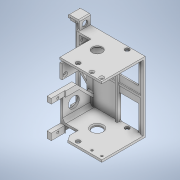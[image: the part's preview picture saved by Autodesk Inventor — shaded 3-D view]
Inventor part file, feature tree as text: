
AUTODESK INVENTOR PART (.ipt)
format: ipt  version: 2021 (Build 250183000, 183)  size: 1,060,352 bytes
history: native  units: mm
features: sketch x66, extrude x55, chamfer x12, hole x11, fillet x7
ambient origin geometry x8: Origin, YZ Plane, XZ Plane, XY Plane, X Axis, Y Axis, Z Axis, Center Point
bodies: Solid1 (feature_tree)
feature tree (151):
  extrude  "Extrusion1"  Depth=48.0mm
  extrude  "Extrusion3"  Depth=2.0mm
  extrude  "Extrusion4"  Depth=2.0mm TaperAngle=0.0deg
  hole  "Hole1"  [1 undecoded]
  hole  "Hole2"  [1 undecoded]
  extrude  "Extrusion5"  Depth=4.0mm
  extrude  "Extrusion6"  Depth=33.0mm
  extrude  "Extrusion7"  Depth=2.0mm
  extrude  "Extrusion8"  Depth=2.0mm TaperAngle=0.0deg
  extrude  "Extrusion9"  Depth=4.0mm
  extrude  "Extrusion10"  Depth=4.0mm
  extrude  "Extrusion11"  Depth=1.0mm
  chamfer  "Chamfer1"  Distance=2.0mm
  fillet  "Fillet1"  Radius=0.4mm
  hole  "Hole3"  [1 undecoded]
  chamfer  "Chamfer2"  Distance=12.4mm
  extrude  "Extrusion12"  Depth=2.0mm TaperAngle=0.0deg
  extrude  "Extrusion13"  Depth=2.0mm TaperAngle=0.0deg
  extrude  "Extrusion14"  Depth=4.4mm
  hole  "Hole4"  [1 undecoded]
  extrude  "Extrusion15"  Depth=2.4mm
  extrude  "Extrusion16"  Depth=1.0mm TaperAngle=45.0deg
  chamfer  "Chamfer3"  Distance=37.6mm
  extrude  "Extrusion17"  Depth=2.0mm TaperAngle=0.0deg
  extrude  "Extrusion18"  Depth=2.4mm
  extrude  "Extrusion19"  Depth=16.0mm
  extrude  "Extrusion20"  Depth=15.0mm
  extrude  "Extrusion21"  Depth=8.0mm TaperAngle=0.0deg
  extrude  "Extrusion22"  Depth=2.0mm TaperAngle=0.0deg
  extrude  "Extrusion23"  Depth=30.0mm
  hole  "Hole5"  [1 undecoded]
  extrude  "Extrusion24"  Depth=20.0mm TaperAngle=0.0deg
  extrude  "Extrusion26"  Depth=2.0mm TaperAngle=0.0deg
  extrude  "Extrusion27"  Depth=9.0mm
  extrude  "Extrusion28"  Depth=3.0mm TaperAngle=0.0deg
  extrude  "Extrusion29"  Depth=6.0mm
  extrude  "Extrusion30"  Depth=2.0mm
  hole  "Hole6"  [1 undecoded]
  chamfer  "Chamfer4"  Distance=17.0mm
  chamfer  "Chamfer5"  Distance=2.0mm
  extrude  "Extrusion32"  Depth=2.0mm
  chamfer  "Chamfer6"  Distance=2.0mm
  extrude  "Extrusion33"  Depth=6.0mm
  fillet  "Fillet2"  Radius=5.0mm
  extrude  "Extrusion34"  TaperAngle=0.0deg  [1 undecoded]
  extrude  "Extrusion35"  Depth=5.0mm TaperAngle=45.0deg
  extrude  "Extrusion36"  Depth=5.0mm
  extrude  "Extrusion37"  Depth=8.0mm TaperAngle=45.0deg
  extrude  "Extrusion38"  Depth=3.0mm
  fillet  "Fillet3"  Radius=10.0mm
  extrude  "Extrusion39"  Depth=10.0mm
  fillet  "Fillet4"  Radius=2.0mm
  extrude  "Extrusion40"  Depth=0.5mm
  extrude  "Extrusion41"  Depth=12.4mm TaperAngle=0.0deg
  extrude  "Extrusion42"  Depth=2.0mm
  extrude  "Extrusion43"  Depth=10.0mm
  hole  "Hole7"  [1 undecoded]
  hole  "Hole8"  [1 undecoded]
  hole  "Hole9"  [1 undecoded]
  hole  "Hole10"  [1 undecoded]
  extrude  "Extrusion44"  Depth=2.0mm TaperAngle=0.0deg
  chamfer  "Chamfer7"  Distance=2.0mm
  extrude  "Extrusion45"  Depth=5.0mm TaperAngle=0.0deg
  extrude  "Extrusion46"  Depth=10.0mm
  extrude  "Extrusion47"  Depth=10.0mm
  extrude  "Extrusion48"  Depth=2.0mm
  extrude  "Extrusion50"  Depth=9.0mm
  fillet  "Fillet7"  Radius=2.2mm
  extrude  "Extrusion52"  Depth=3.0mm
  chamfer  "Chamfer9"  Distance=3.0mm
  chamfer  "Chamfer10"  Distance=3.0mm
  chamfer  "Chamfer11"  Distance=3.0mm
  extrude  "Extrusion54"  Depth=3.0mm
  extrude  "Extrusion55"  Depth=12.0mm
  extrude  "Extrusion56"  Depth=5.2mm
  extrude  "Extrusion57"  Depth=1.2mm
  chamfer  "Chamfer12"  Distance=1.0mm
  extrude  "Extrusion58"  Depth=1.0mm
  extrude  "Extrusion59"  Depth=2.0mm TaperAngle=0.0deg
  fillet  "Fillet9"  Radius=1.2mm
  hole  "Hole11"  [1 undecoded]
  fillet  "Fillet10"  Radius=81.0mm
  chamfer  "Chamfer13"  Distance=10.0mm
  extrude  "Extrusion60"  Depth=0.5mm
  extrude  "Extrusion61"  Depth=0.5mm
  sketch  "Sketch1"  dims[d0=48.0mm d1=60.0mm]
  sketch  "Sketch3"  dims[d2=1.2mm d3=0.0mm d6=2.0mm]
  sketch  "Sketch4"  dims[d7=2.0mm d8=40.0mm d9=0.0mm]
  sketch  "Sketch5"  dims[d10=16.8mm d11=21.0mm]
  sketch  "Sketch6"  dims[d12=9.2mm d13=80.0mm d14=0.0mm]
  sketch  "Sketch7"  dims[d15=4.0mm d16=22.7mm]
  sketch  "Sketch8"  dims[d17=11.8mm d18=33.0mm]
  sketch  "Sketch9"  dims[d19=4.0mm d20=6.0mm d21=6.0mm d22=2.0mm d23=90.0deg d24=4.0mm d25=20.594885mm]
  sketch  "Sketch10"  dims[d26=4.0mm d27=6.0mm d28=6.0mm d29=2.0mm d30=90.0deg d31=4.0mm d32=20.594885mm d33=2.0mm]
  sketch  "Sketch11"  dims[d34=2.0mm d35=0.8mm d36=0.0mm]
  sketch  "Sketch12"  dims[d37=4.0mm d38=4.0mm]
  sketch  "Sketch13"  dims[d39=1.0mm d40=4.0mm]
  sketch  "Sketch14"  dims[d41=4.0mm d42=1.0mm]
  sketch  "Sketch15"  dims[d43=3.0mm d44=2.0mm d45=0.0mm d46=0.4mm d47=0.0mm]
  sketch  "Sketch16"  dims[d48=12.0mm d49=22.0mm]
  sketch  "Sketch17"  dims[d50=12.4mm d51=12.4mm d52=0.0mm]
  sketch  "Sketch18"  dims[d53=8.0mm d54=2.0mm d55=0.0mm]
  sketch  "Sketch19"  dims[d56=8.0mm d57=2.0mm d58=0.0mm]
  sketch  "Sketch20"  dims[d59=0.4mm d60=4.4mm]
  sketch  "Sketch21"  dims[d61=12.4mm d62=0.0mm d63=2.4mm d64=2.0mm d65=45.0deg]
  sketch  "Sketch22"  dims[d66=2.0mm d67=2.4mm]
  sketch  "Sketch23"  dims[d68=6.0mm]
  sketch  "Sketch24"  dims[d69=2.0mm d70=6.0mm d71=3.0mm d72=2.0mm d73=90.0deg d74=5.0mm d75=20.594885mm d76=1.0mm d77=2.0mm d78=45.0deg]
  sketch  "Sketch25"  dims[d79=22.0mm]
  sketch  "Sketch26"  dims[d80=5.0mm]
  sketch  "Sketch27"  dims[d81=4.4mm]
  sketch  "Sketch28"  dims[d82=4.4mm d83=37.6mm d84=0.0mm]
  sketch  "Sketch29"  dims[d85=4.4mm d86=0.0mm d87=2.0mm d88=0.0mm]
  sketch  "Sketch31"  dims[d89=6.0mm d90=2.4mm]
  sketch  "Sketch32"  dims[d91=27.2mm]
  sketch  "Sketch33"  dims[d92=2.0mm d93=6.0mm d94=3.0mm d95=2.0mm d96=90.0deg d97=5.0mm d98=20.594885mm d99=16.0mm]
  sketch  "Sketch34"  dims[d100=2.0mm d101=0.0mm d102=15.0mm]
  sketch  "Sketch35"  dims[d103=8.0mm d104=20.0mm d105=0.0mm]
  sketch  "Sketch36"  dims[d106=2.0mm d107=2.0mm d108=45.0deg d109=0.8mm d110=0.0mm]
  sketch  "Sketch38"  dims[d111=60.0mm d112=30.0mm]
  sketch  "Sketch39"  dims[d113=1.0mm d114=1.0mm]
  sketch  "Sketch40"  dims[d115=0.8mm d116=0.0mm d117=20.0mm d118=0.0mm]
  sketch  "Sketch41"  dims[d119=20.0mm d120=0.0mm d121=2.0mm d122=0.0mm]
  sketch  "Sketch42"  dims[d123=17.0mm d124=9.0mm]
  sketch  "Sketch43"  dims[d125=10.0mm d126=0.0mm d127=3.0mm d128=0.0mm]
  sketch  "Sketch44"  dims[d129=6.0mm d130=9.6mm]
  sketch  "Sketch45"  dims[d131=2.0mm d132=6.0mm d133=3.0mm d134=2.0mm d135=90.0deg d136=5.0mm d137=20.594885mm d138=2.0mm]
  sketch  "Sketch46"  dims[d139=2.0mm d140=10.0mm d141=0.0mm]
  sketch  "Sketch47"  dims[d145=0.2mm d146=17.0mm d147=0.0mm d148=2.0mm d149=0.0mm]
  sketch  "Sketch48"  dims[d150=11.7mm d151=28.0mm d152=2.0mm d153=0.0mm]
  sketch  "Sketch49"  dims[d154=2.0mm d155=6.0mm d156=5.0mm d157=0.0mm]
  sketch  "Sketch50"  dims[d158=33.4mm d159=0.0mm d160=0.0mm]
  sketch  "Sketch51"  dims[d161=27.2mm]
  sketch  "Sketch52"  dims[d162=2.0mm d163=6.0mm d164=3.0mm d165=2.0mm d166=90.0deg d167=5.0mm d168=20.594885mm d169=5.0mm d170=2.0mm d171=45.0deg]
  sketch  "Sketch53"  dims[d172=5.6mm d173=2.0mm d174=45.0deg d181=5.0mm]
  sketch  "Sketch54"  dims[d182=2.0mm d183=0.0mm d184=8.0mm d185=2.0mm d186=45.0deg]
  sketch  "Sketch55"  dims[d187=20.0mm d188=0.0mm d189=3.0mm d190=10.0mm]
  sketch  "Sketch56"  dims[d191=10.0mm d192=10.0mm d193=2.0mm d194=0.0mm]
  sketch  "Sketch57"  dims[d195=23.0mm d196=0.5mm]
  sketch  "Sketch58"  dims[d197=0.5mm d198=12.4mm d199=0.0mm]
  sketch  "Sketch60"  dims[d200=10.0mm d201=0.0mm d202=2.0mm]
  sketch  "Sketch62"  dims[d203=2.4mm d204=0.0mm d205=10.0mm]
  sketch  "Sketch64"  dims[d206=5.0mm d207=5.0mm d208=0.0mm]
  sketch  "Sketch65"  dims[d209=1.0mm d210=4.0mm]
  sketch  "Sketch66"  dims[d211=4.0mm d212=20.0mm]
  sketch  "Sketch67"  dims[d213=4.0mm d214=4.0mm]
  sketch  "Sketch68"  dims[d215=20.0mm d216=2.0mm d217=0.0mm]
  sketch  "Sketch69"  dims[d218=1.0mm]
  sketch  "Sketch70"  dims[d219=2.0mm d220=2.0mm d221=0.0mm]
  sketch  "Sketch71"  dims[d222=2.0mm d223=0.0mm d224=5.0mm d225=0.0mm]
  sketch  "Sketch72"  dims[d226=5.0mm d227=0.0mm d228=10.0mm d229=10.0mm d230=2.0mm d231=9.0mm d232=2.2mm d233=2.0mm d234=6.0mm d235=4.0mm d236=2.0mm d237=90.0deg d238=3.0mm d239=20.594885mm d240=3.0mm d241=3.0mm d242=2.0mm d243=6.0mm d244=4.0mm d245=2.0mm d246=90.0deg d247=3.0mm d248=20.594885mm d249=3.0mm d250=3.0mm d251=3.0mm d252=12.0mm d253=2.0mm d254=6.0mm d255=4.0mm d256=2.0mm d257=90.0deg d258=3.0mm d259=20.594885mm d260=2.0mm d261=6.0mm d262=4.0mm d263=2.0mm d264=90.0deg d265=3.0mm d266=20.594885mm d267=5.2mm d268=1.2mm d269=1.0mm d270=1.0mm d271=2.0mm d272=0.0mm d273=1.2mm d274=2.0mm d275=45.0deg d276=2.0mm d277=0.0mm d278=81.0mm d279=10.0mm d280=70.0mm d281=8.5mm d282=2.0mm d283=2.0mm d284=2.0mm d285=64.0mm d286=8.5mm d287=2.0mm d288=0.0mm d289=21.4mm d290=2.0mm d291=0.0mm d295=5.0mm d296=5.0mm d297=40.5mm d298=5.0mm d299=5.0mm d300=76.03mm d301=2.0mm d302=2.0mm d303=2.0mm d304=2.0mm d305=2.0mm d306=2.0mm d307=2.0mm d308=2.0mm d309=2.0mm d310=2.0mm d311=2.0mm d312=2.0mm d313=6.0mm d314=0.0mm d322=2.0mm d323=0.0mm d331=1.0mm d332=2.0mm d333=0.0mm d334=4.0mm d335=2.0mm d336=45.0deg d337=2.0mm d338=2.0mm d339=45.0deg d343=1.0mm d344=2.0mm d345=45.0deg d346=2.0mm d347=0.0mm d348=2.0mm d349=8.0mm d350=0.0mm d351=5.0mm d352=2.0mm d353=0.0mm d354=5.0mm d355=4.0mm d356=0.0mm d357=1.2mm d358=2.0mm d359=45.0deg d360=2.0mm d361=0.0mm d362=1.0mm d363=0.0mm d364=1.0mm d365=2.5mm d366=2.5mm d367=4.0mm d368=13.0mm d369=2.0mm d370=2.5mm d371=2.0mm d372=6.0mm d373=4.0mm d374=2.0mm d375=90.0deg d376=3.0mm d377=20.594885mm d378=1.0mm d379=1.2mm d380=2.0mm d381=45.0deg d382=2.0mm d383=2.0mm d384=14.0mm d385=2.0mm d386=0.0mm d387=0.6mm d388=12.4mm d389=0.0mm d324=0.5mm d325=0.872665mm d326=0.5mm d327=0.872665mm]
note: 12 required parameter values undecoded (feature->parameter linkage not recoverable at this tier; creation-order binding heuristic only, values carry confidence <= 0.55)
